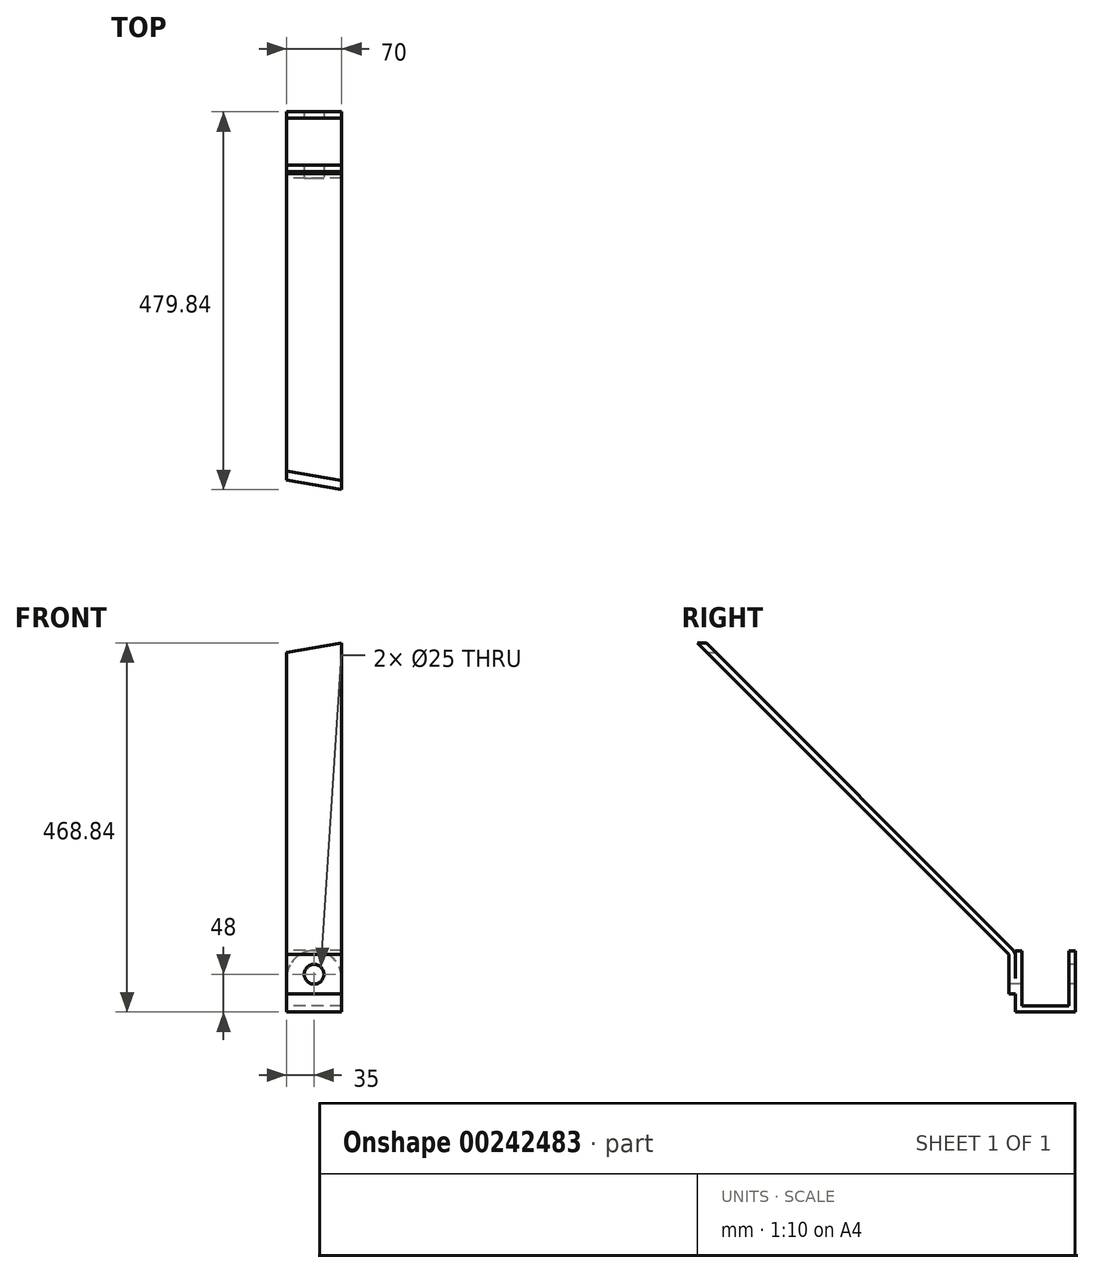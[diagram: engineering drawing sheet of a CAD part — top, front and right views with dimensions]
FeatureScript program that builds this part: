
annotation { "Feature Type Name" : "Feature", "Feature Type Description" : "" }
export const myFeature = defineFeature(function(context is Context, id is Id, definition is map)
    precondition{}
    {
        {
            var Q0;
            Q0=qCreatedBy(makeId("Top.planeOp"),FACE);
            var sketch = newSketch(context, id + "F0", { "sketchPlane" : qUnion([Q0])});
            skLineSegment(sketch, "E0.bottom", {"start": v(35, 38) * mm, "end": v(-35, 38) * mm});
            skLineSegment(sketch, "E0.top", {"start": v(35, -38) * mm, "end": v(-35, -38) * mm});
            skLineSegment(sketch, "E0.left", {"start": v(35, 38) * mm, "end": v(35, -38) * mm});
            skLineSegment(sketch, "E0.right", {"start": v(-35, 38) * mm, "end": v(-35, -38) * mm});
            skPoint(sketch, "E0.middle", {"position": v(0, 0) * mm});
            skSolve(sketch);
        }
        {
            var Q0;
            Q0=makeQuery(id+"F0.imprint","IMPRINT",FACE,{"disambiguationData":[TD([[makeQuery(id+"F0.imprint","IMPRINT",EDGE,{"derivedFrom":sQuery(id+"F0.wireOp",EDGE,"E0.bottom")}),1.0]])]});
            extrude(context, id + "F1", {"entities" : qUnion([Q0]), "depth" : 8 * mm});
        }
        {
            var Q0;
            Q0=makeQuery(id+"F1.opExtrude","CAP_FACE",FACE,{"disambiguationData":[OSD([sQuery(id+"F0.wireOp",EDGE,"E0.bottom"),sQuery(id+"F0.wireOp",EDGE,"E0.top"),sQuery(id+"F0.wireOp",EDGE,"E0.left"),sQuery(id+"F0.wireOp",EDGE,"E0.right")])],"isStart":false});
            var sketch = newSketch(context, id + "F2", { "sketchPlane" : qUnion([Q0])});
            skLineSegment(sketch, "E1.bottom", {"start": v(-35, -38) * mm, "end": v(35, -38) * mm});
            skLineSegment(sketch, "E1.top", {"start": v(-35, -30) * mm, "end": v(35, -30) * mm});
            skLineSegment(sketch, "E1.left", {"start": v(-35, -38) * mm, "end": v(-35, -30) * mm});
            skLineSegment(sketch, "E1.right", {"start": v(35, -38) * mm, "end": v(35, -30) * mm});
            skLineSegment(sketch, "E2.bottom", {"start": v(35, 38) * mm, "end": v(-35, 38) * mm});
            skLineSegment(sketch, "E2.top", {"start": v(35, 30) * mm, "end": v(-35, 30) * mm});
            skLineSegment(sketch, "E2.left", {"start": v(35, 38) * mm, "end": v(35, 30) * mm});
            skLineSegment(sketch, "E2.right", {"start": v(-35, 38) * mm, "end": v(-35, 30) * mm});
            skSolve(sketch);
        }
        {
            var Q0;
            Q0=makeQuery(id+"F2.imprint","IMPRINT",FACE,{"disambiguationData":[TD([[makeQuery(id+"F2.imprint","IMPRINT",EDGE,{"derivedFrom":sQuery(id+"F2.wireOp",EDGE,"E1.bottom")}),-1.0]])]});
            var Q1;
            Q1=makeQuery(id+"F2.imprint","IMPRINT",FACE,{"disambiguationData":[TD([[makeQuery(id+"F2.imprint","IMPRINT",EDGE,{"derivedFrom":sQuery(id+"F2.wireOp",EDGE,"E2.bottom")}),1.0]])]});
            extrude(context, id + "F3", {"entities" : qUnion([Q0, Q1]), "operationType" : NewBodyOperationType.ADD, "depth" : 70 * mm});
        }
        {
            var Q0;
            Q0=makeQuery(id+"F3.boolean.opBoolean","MERGE",FACE,{"derivedFrom":[makeQuery(id+"F1.opExtrude","SWEPT_FACE",FACE,{"disambiguationData":[OSD([sQuery(id+"F0.wireOp",EDGE,"E0.top")])]}),makeQuery(id+"F3.opExtrude","SWEPT_FACE",FACE,{"disambiguationData":[OSD([sQuery(id+"F2.wireOp",EDGE,"E1.bottom")])]})]});
            var sketch = newSketch(context, id + "F4", { "sketchPlane" : qUnion([Q0])});
            skCircle(sketch, "E3", {"center": v(0, 48) * mm, "radius": 12.5 * mm});
            skSolve(sketch);
        }
        {
            var Q0;
            Q0=makeQuery(id+"F4.imprint","IMPRINT",FACE,{"disambiguationData":[TD([[makeQuery(id+"F4.imprint","IMPRINT",EDGE,{"derivedFrom":sQuery(id+"F4.wireOp",EDGE,"E3")}),1.0]])]});
            extrude(context, id + "F5", {"entities" : qUnion([Q0]), "operationType" : NewBodyOperationType.REMOVE, "oppositeDirection" : true, "depth" : 80 * mm});
        }
        {
            var Q0;
            Q0=makeQuery(id+"F3.opExtrude","CAP_EDGE",EDGE,{"disambiguationData":[OSD([sQuery(id+"F2.wireOp",EDGE,"E1.right")])],"isStart":false});
            var Q1;
            Q1=makeQuery(id+"F3.opExtrude","CAP_EDGE",EDGE,{"disambiguationData":[OSD([sQuery(id+"F2.wireOp",EDGE,"E1.left")])],"isStart":false});
            var Q2;
            Q2=makeQuery(id+"F3.opExtrude","CAP_EDGE",EDGE,{"disambiguationData":[OSD([sQuery(id+"F2.wireOp",EDGE,"E2.left")])],"isStart":false});
            var Q3;
            Q3=makeQuery(id+"F3.opExtrude","CAP_EDGE",EDGE,{"disambiguationData":[OSD([sQuery(id+"F2.wireOp",EDGE,"E2.right")])],"isStart":false});
            fillet(context, id + "F6", {"entities" : qUnion([Q0, Q1, Q2, Q3]), "radius" : 35 * mm, "tangentPropagation" : true, "allowEdgeOverflow" : false});
        }
        {
            var Q0;
            Q0=makeQuery(id+"F3.boolean.opBoolean","MERGE",FACE,{"derivedFrom":[makeQuery(id+"F1.opExtrude","SWEPT_FACE",FACE,{"disambiguationData":[OSD([sQuery(id+"F0.wireOp",EDGE,"E0.top")])]}),makeQuery(id+"F3.opExtrude","SWEPT_FACE",FACE,{"disambiguationData":[OSD([sQuery(id+"F2.wireOp",EDGE,"E1.bottom")])]})]});
            var sketch = newSketch(context, id + "F7", { "sketchPlane" : qUnion([Q0])});
            skCircle(sketch, "E4.0", {"center": v(0, 48) * mm, "radius": 12.5 * mm});
            skLineSegment(sketch, "E5.bottom", {"start": v(35, 73) * mm, "end": v(-35, 73) * mm});
            skLineSegment(sketch, "E5.top", {"start": v(35, 23) * mm, "end": v(-35, 23) * mm});
            skLineSegment(sketch, "E5.left", {"start": v(35, 73) * mm, "end": v(35, 23) * mm});
            skLineSegment(sketch, "E5.right", {"start": v(-35, 73) * mm, "end": v(-35, 23) * mm});
            skSolve(sketch);
        }
        {
            var Q0;
            Q0=makeQuery(id+"F7.imprint","IMPRINT",FACE,{"disambiguationData":[TD([[makeQuery(id+"F7.imprint","IMPRINT",EDGE,{"derivedFrom":sQuery(id+"F7.wireOp",EDGE,"E4.0")}),-1.0]])]});
            var Q1;
            {var subQ0=sQuery(id+"F7.wireOp",EDGE,"E5.left");var subQ1=sQuery(id+"F7.wireOp",EDGE,"E5.bottom");var subQ2=makeQuery(id+"F7.imprint","INTERSECT",VERTEX,{"derivedFrom":[subQ1,subQ0]});Q1=makeQuery(id+"F7.imprint","IMPRINT",FACE,{"disambiguationData":[TD([[makeQuery(id+"F7.imprint","IMPRINT",EDGE,{"disambiguationData":[TD([[subQ2,-1.0]])],"derivedFrom":subQ1}),1.0]])]});}
            var Q2;
            {var subQ0=sQuery(id+"F7.wireOp",EDGE,"E5.right");var subQ1=sQuery(id+"F7.wireOp",EDGE,"E5.bottom");var subQ2=makeQuery(id+"F7.imprint","INTERSECT",VERTEX,{"derivedFrom":[subQ1,subQ0]});Q2=makeQuery(id+"F7.imprint","IMPRINT",FACE,{"disambiguationData":[TD([[makeQuery(id+"F7.imprint","IMPRINT",EDGE,{"disambiguationData":[TD([[subQ2,1.0]])],"derivedFrom":subQ1}),1.0]])]});}
            extrude(context, id + "F8", {"entities" : qUnion([Q0, Q1, Q2]), "depth" : 8 * mm});
        }
        {
            var Q0;
            Q0=makeQuery(id+"F8.opExtrude","SWEPT_FACE",FACE,{"disambiguationData":[OSD([sQuery(id+"F7.wireOp",EDGE,"E5.right")])]});
            var sketch = newSketch(context, id + "F9", { "sketchPlane" : qUnion([Q0])});
            skLineSegment(sketch, "E6", {"start": v(46, 73) * mm, "end": v(40.34, 78.66) * mm});
            skLineSegment(sketch, "E7", {"start": v(40.34, 78.66) * mm, "end": v(38, 73) * mm});
            skSolve(sketch);
        }
        {
            var Q0;
            Q0=makeQuery(id+"F9.imprint","IMPRINT",FACE,{"disambiguationData":[TD([[makeQuery(id+"F9.imprint","IMPRINT",EDGE,{"derivedFrom":sQuery(id+"F9.wireOp",EDGE,"E6")}),1.0]])]});
            extrude(context, id + "F10", {"entities" : qUnion([Q0]), "operationType" : NewBodyOperationType.ADD, "oppositeDirection" : true, "depth" : 70 * mm});
        }
        {
            var Q0;
            Q0=makeQuery(id+"F10.opExtrude","SWEPT_FACE",FACE,{"disambiguationData":[OSD([sQuery(id+"F9.wireOp",EDGE,"E6")])]});
            var sketch = newSketch(context, id + "F11", { "sketchPlane" : qUnion([Q0])});
            skLineSegment(sketch, "E8.0.0", {"start": v(-35, 27.1) * mm, "end": v(-35, 19.1) * mm});
            skLineSegment(sketch, "E8.0.1", {"start": v(-35, 19.1) * mm, "end": v(35, 19.1) * mm});
            skLineSegment(sketch, "E8.0.2", {"start": v(35, 19.1) * mm, "end": v(35, 27.1) * mm});
            skLineSegment(sketch, "E8.0.3", {"start": v(35, 27.1) * mm, "end": v(-35, 27.1) * mm});
            skSolve(sketch);
        }
        {
            var Q0;
            Q0=makeQuery(id+"F11.imprint","IMPRINT",FACE,{"disambiguationData":[TD([[makeQuery(id+"F11.imprint","IMPRINT",EDGE,{"derivedFrom":sQuery(id+"F11.wireOp",EDGE,"E8.0.0")}),-1.0]])]});
            extrude(context, id + "F12", {"entities" : qUnion([Q0]), "operationType" : NewBodyOperationType.ADD, "depth" : 1000 * mm});
        }
        {
            var Q0;
            {var subQ0=sQuery(id+"F7.wireOp",EDGE,"E5.right");Q0=makeQuery(id+"F12.boolean.opBoolean","MERGE",FACE,{"derivedFrom":[makeQuery(id+"F10.boolean.opBoolean","MERGE",FACE,{"derivedFrom":[makeQuery(id+"F8.opExtrude","SWEPT_FACE",FACE,{"disambiguationData":[OSD([subQ0])]}),makeQuery(id+"F10.opExtrude","CAP_FACE",FACE,{"disambiguationData":[OSD([sQuery(id+"F7.wireOp",EDGE,"E5.bottom"),subQ0,sQuery(id+"F9.wireOp",EDGE,"E6"),sQuery(id+"F9.wireOp",EDGE,"E7")])],"isStart":true})]}),makeQuery(id+"F12.opExtrude","SWEPT_FACE",FACE,{"disambiguationData":[OSD([sQuery(id+"F11.wireOp",EDGE,"E8.0.0")])]})]});}
            var sketch = newSketch(context, id + "F13", { "sketchPlane" : qUnion([Q0])});
            skLineSegment(sketch, "E9", {"start": v(268.24, 523.32) * mm, "end": v(805.33, 884.72) * mm});
            skLineSegment(sketch, "E10", {"start": v(805.33, 884.72) * mm, "end": v(775.65, 537.5) * mm});
            skLineSegment(sketch, "E11", {"start": v(775.65, 537.5) * mm, "end": v(624.15, 523.32) * mm});
            skLineSegment(sketch, "E12", {"start": v(30, 78) * mm, "end": v(38, 78) * mm});
            skLineSegment(sketch, "E13.0", {"start": v(747.45, 785.76) * mm, "end": v(40.34, 78.66) * mm});
            skLineSegment(sketch, "E14", {"start": v(30, 451.5) * mm, "end": v(392.92, 451.5) * mm});
            skLineSegment(sketch, "E15", {"start": v(581.23, 451.5) * mm, "end": v(624.15, 523.32) * mm});
            skLineSegment(sketch, "E16", {"start": v(30, 451.5) * mm, "end": v(268.24, 523.32) * mm});
            skLineSegment(sketch, "E17", {"start": v(392.92, 451.5) * mm, "end": v(392.92, 456.5) * mm});
            skLineSegment(sketch, "E18", {"start": v(446.28, 456.5) * mm, "end": v(392.92, 456.5) * mm});
            skLineSegment(sketch, "E19", {"start": v(446.28, 456.5) * mm, "end": v(446.28, 451.5) * mm});
            skLineSegment(sketch, "E20.trimOffspring", {"start": v(446.28, 451.5) * mm, "end": v(581.23, 451.5) * mm});
            skSolve(sketch);
        }
        {
            var Q0;
            {var subQ1=sQuery(id+"F11.wireOp",EDGE,"E8.0.0");var subQ6=makeQuery(id+"F12.opExtrude","CAP_EDGE",EDGE,{"disambiguationData":[OSD([subQ1])],"isStart":false});Q0=makeQuery(id+"F13.imprint","IMPRINT",FACE,{"disambiguationData":[TD([[makeQuery(id+"F13.imprint","IMPRINT",EDGE,{"derivedFrom":subQ6}),1.0]])]});}
            extrude(context, id + "F14", {"entities" : qUnion([Q0]), "operationType" : NewBodyOperationType.REMOVE, "oppositeDirection" : true, "depth" : 70 * mm});
        }
        {
            var Q0;
            Q0=qCreatedBy(makeId("Front.planeOp"),FACE);
            var sketch = newSketch(context, id + "F15", { "sketchPlane" : qUnion([Q0])});
            skLineSegment(sketch, "E21.0.0", {"start": v(-35, 456.5) * mm, "end": v(35, 456.5) * mm});
            skLineSegment(sketch, "E21.0.1", {"start": v(35, 456.5) * mm, "end": v(35, 78.66) * mm});
            skLineSegment(sketch, "E21.0.2", {"start": v(35, 78.66) * mm, "end": v(-35, 78.66) * mm});
            skLineSegment(sketch, "E21.0.3", {"start": v(-35, 78.66) * mm, "end": v(-35, 456.5) * mm});
            skLineSegment(sketch, "E22", {"start": v(35, 456.5) * mm, "end": v(35, 468.84) * mm});
            skLineSegment(sketch, "E23", {"start": v(-35, 456.5) * mm, "end": v(35, 468.84) * mm});
            skSolve(sketch);
        }
        {
            var Q0;
            Q0=makeQuery(id+"F15.imprint","IMPRINT",FACE,{"disambiguationData":[TD([[makeQuery(id+"F15.imprint","IMPRINT",EDGE,{"derivedFrom":sQuery(id+"F15.wireOp",EDGE,"E21.0.0")}),1.0]])]});
            extrude(context, id + "F16", {"entities" : qUnion([Q0]), "operationType" : NewBodyOperationType.ADD, "depth" : 800 * mm});
        }
        {
            var Q0;
            Q0=makeQuery(id+"F16.boolean.opBoolean","MERGE",FACE,{"derivedFrom":[makeQuery(id+"F12.boolean.opBoolean","MERGE",FACE,{"derivedFrom":[makeQuery(id+"F10.boolean.opBoolean","MERGE",FACE,{"derivedFrom":[makeQuery(id+"F8.opExtrude","SWEPT_FACE",FACE,{"disambiguationData":[OSD([sQuery(id+"F7.wireOp",EDGE,"E5.left")])]}),makeQuery(id+"F10.opExtrude","CAP_FACE",FACE,{"disambiguationData":[OSD([sQuery(id+"F7.wireOp",EDGE,"E5.bottom"),sQuery(id+"F7.wireOp",EDGE,"E5.right"),sQuery(id+"F9.wireOp",EDGE,"E6"),sQuery(id+"F9.wireOp",EDGE,"E7")])],"isStart":false})]}),makeQuery(id+"F12.opExtrude","SWEPT_FACE",FACE,{"disambiguationData":[OSD([sQuery(id+"F11.wireOp",EDGE,"E8.0.2")])]})]}),makeQuery(id+"F16.opExtrude","SWEPT_FACE",FACE,{"disambiguationData":[OSD([sQuery(id+"F15.wireOp",EDGE,"E22")])]})]});
            var sketch = newSketch(context, id + "F17", { "sketchPlane" : qUnion([Q0])});
            skLineSegment(sketch, "E24.0.0", {"start": v(-40.34, 78.66) * mm, "end": v(-418.19, 456.5) * mm});
            skLineSegment(sketch, "E24.0.1", {"start": v(-418.19, 456.5) * mm, "end": v(0, 456.5) * mm});
            skLineSegment(sketch, "E24.0.2", {"start": v(0, 456.5) * mm, "end": v(0, 468.84) * mm});
            skLineSegment(sketch, "E24.0.3", {"start": v(0, 468.84) * mm, "end": v(-800, 468.84) * mm});
            skLineSegment(sketch, "E24.0.4", {"start": v(-800, 468.84) * mm, "end": v(-800, 456.5) * mm});
            skLineSegment(sketch, "E24.0.5", {"start": v(-800, 456.5) * mm, "end": v(-429.5, 456.5) * mm});
            skLineSegment(sketch, "E24.0.6", {"start": v(-429.5, 456.5) * mm, "end": v(-46, 73) * mm});
            skLineSegment(sketch, "E24.0.7", {"start": v(-46, 73) * mm, "end": v(-46, 23) * mm});
            skLineSegment(sketch, "E24.0.8", {"start": v(-46, 23) * mm, "end": v(-38, 23) * mm});
            skLineSegment(sketch, "E24.0.9", {"start": v(-38, 23) * mm, "end": v(-38, 73) * mm});
            skLineSegment(sketch, "E24.0.10", {"start": v(-38, 73) * mm, "end": v(-40.34, 78.66) * mm});
            skLineSegment(sketch, "E25", {"start": v(-421.64, 448.64) * mm, "end": v(-441.84, 468.84) * mm});
            skLineSegment(sketch, "E26", {"start": v(-413.12, 451.43) * mm, "end": v(-430.53, 468.84) * mm});
            skLineSegment(sketch, "E27", {"start": v(-430.53, 468.84) * mm, "end": v(-441.84, 468.84) * mm});
            skSolve(sketch);
        }
        {
            var Q0;
            {var subQ0=sQuery(id+"F17.wireOp",EDGE,"E25");Q0=makeQuery(id+"F17.imprint","IMPRINT",FACE,{"disambiguationData":[TD([[makeQuery(id+"F17.imprint","IMPRINT",EDGE,{"derivedFrom":subQ0}),1.0]])]});}
            var Q1;
            {var subQ0=sQuery(id+"F17.wireOp",EDGE,"E26");Q1=makeQuery(id+"F17.imprint","IMPRINT",FACE,{"disambiguationData":[TD([[makeQuery(id+"F17.imprint","IMPRINT",EDGE,{"derivedFrom":subQ0}),-1.0]])]});}
            extrude(context, id + "F18", {"entities" : qUnion([Q0, Q1]), "operationType" : NewBodyOperationType.REMOVE, "oppositeDirection" : true, "depth" : 100 * mm});
        }
    });
